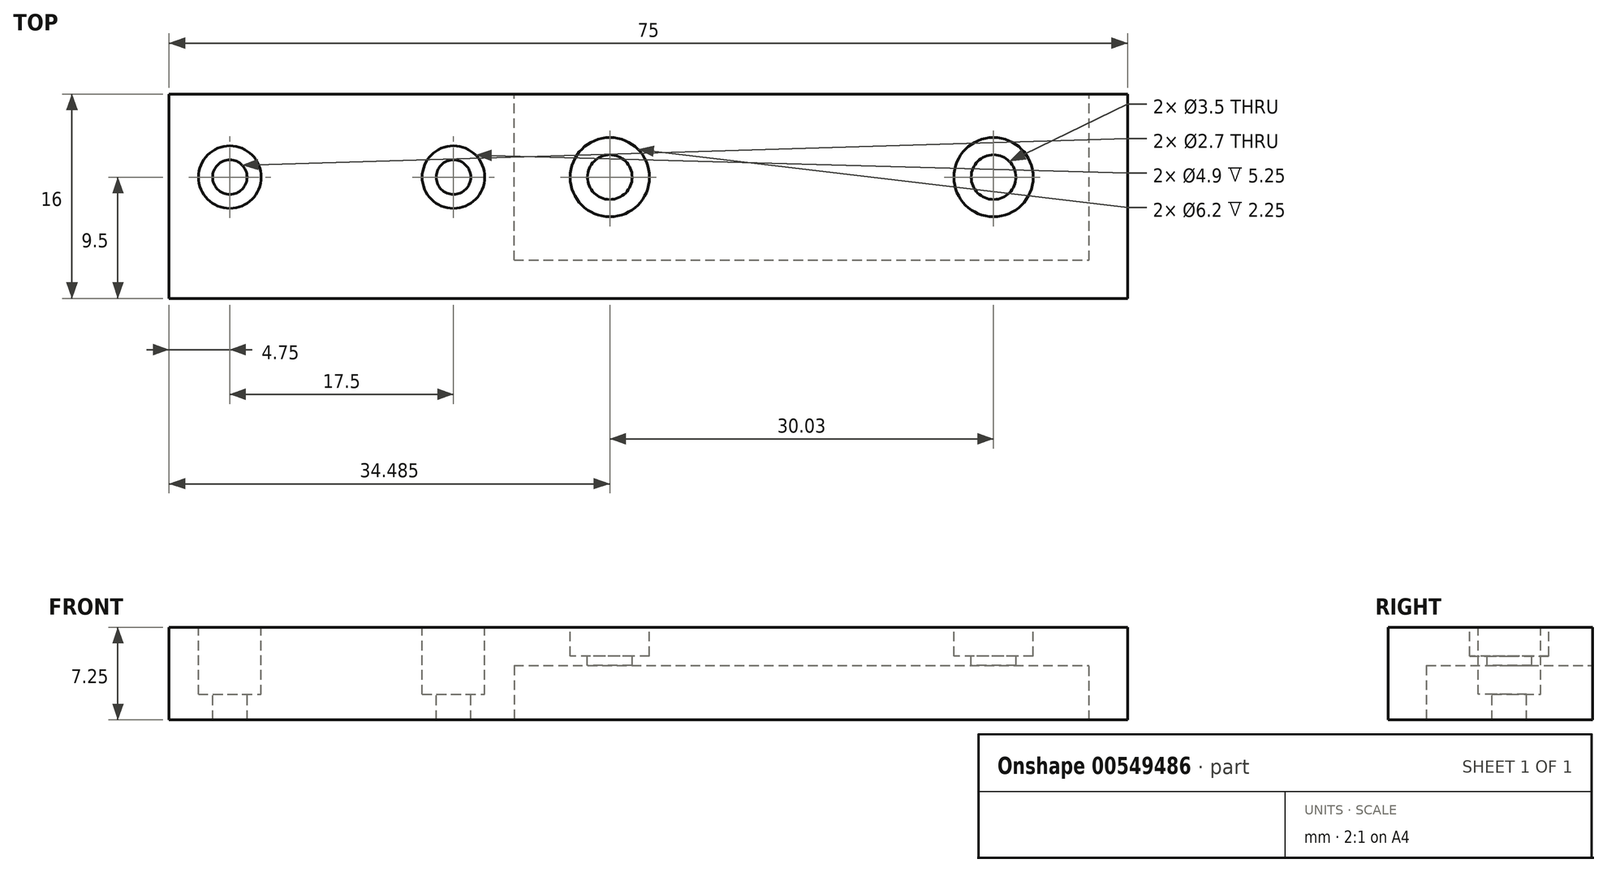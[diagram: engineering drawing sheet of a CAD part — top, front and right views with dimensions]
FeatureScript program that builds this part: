
annotation { "Feature Type Name" : "Feature", "Feature Type Description" : "" }
export const myFeature = defineFeature(function(context is Context, id is Id, definition is map)
    precondition{}
    {
        {
            var Q0;
            Q0=qCreatedBy(makeId("Front.planeOp"),FACE);
            var sketch = newSketch(context, id + "F0", { "sketchPlane" : qUnion([Q0])});
            skLineSegment(sketch, "E0", {"start": v(0, 0) * mm, "end": v(0, -4.25) * mm});
            skLineSegment(sketch, "E1", {"start": v(0, -4.25) * mm, "end": v(-27, -4.25) * mm});
            skLineSegment(sketch, "E2", {"start": v(0, 0) * mm, "end": v(45, 0) * mm});
            skLineSegment(sketch, "E3", {"start": v(45, 0) * mm, "end": v(45, 3) * mm});
            skLineSegment(sketch, "E4", {"start": v(45, 3) * mm, "end": v(0, 3) * mm});
            skLineSegment(sketch, "E5", {"start": v(0, 3) * mm, "end": v(-27, 3) * mm});
            skLineSegment(sketch, "E6", {"start": v(-27, 3) * mm, "end": v(-27, -4.25) * mm});
            skSolve(sketch);
        }
        {
            var Q0;
            Q0=makeQuery(id+"F0.imprint","IMPRINT",FACE,{"disambiguationData":[TD([[makeQuery(id+"F0.imprint","IMPRINT",EDGE,{"derivedFrom":sQuery(id+"F0.wireOp",EDGE,"E0")}),-1.0]])]});
            extrude(context, id + "F1", {"entities" : qUnion([Q0]), "depth" : 13 * mm, "offsetDistance" : 25 * mm});
        }
        {
            var Q0;
            Q0=makeQuery(id+"F1.opExtrude","SWEPT_FACE",FACE,{"disambiguationData":[OSD([sQuery(id+"F0.wireOp",EDGE,"E4"),sQuery(id+"F0.wireOp",EDGE,"E5")])]});
            var sketch = newSketch(context, id + "F2", { "sketchPlane" : qUnion([Q0])});
            skLineSegment(sketch, "E7", {"start": v(0, 0) * mm, "end": v(0, -13) * mm, "construction": true});
            skCircle(sketch, "E8", {"center": v(-22.25, -6.5) * mm, "radius": 1.35 * mm});
            skCircle(sketch, "E9", {"center": v(-4.75, -6.5) * mm, "radius": 1.35 * mm});
            skCircle(sketch, "E10", {"center": v(7.48, -6.5) * mm, "radius": 1.75 * mm});
            skCircle(sketch, "E11", {"center": v(37.52, -6.5) * mm, "radius": 1.75 * mm});
            skCircle(sketch, "E12", {"center": v(-22.25, -6.5) * mm, "radius": 2.45 * mm});
            skCircle(sketch, "E13", {"center": v(-4.75, -6.5) * mm, "radius": 2.45 * mm});
            skLineSegment(sketch, "E14", {"start": v(-4.75, -6.5) * mm, "end": v(0, -6.5) * mm, "construction": true});
            skLineSegment(sketch, "E15", {"start": v(-27, -6.5) * mm, "end": v(-22.25, -6.5) * mm, "construction": true});
            skCircle(sketch, "E16", {"center": v(7.48, -6.5) * mm, "radius": 3.1 * mm});
            skCircle(sketch, "E17", {"center": v(37.52, -6.5) * mm, "radius": 3.1 * mm});
            skLineSegment(sketch, "E18", {"start": v(0, -6.5) * mm, "end": v(7.48, -6.5) * mm, "construction": true});
            skLineSegment(sketch, "E19", {"start": v(37.52, -6.5) * mm, "end": v(45, -6.5) * mm, "construction": true});
            skSolve(sketch);
        }
        {
            var Q0;
            Q0=makeQuery(id+"F2.imprint","IMPRINT",FACE,{"disambiguationData":[TD([[makeQuery(id+"F2.imprint","IMPRINT",EDGE,{"derivedFrom":sQuery(id+"F2.wireOp",EDGE,"E9")}),1.0]])]});
            var Q1;
            Q1=makeQuery(id+"F2.imprint","IMPRINT",FACE,{"disambiguationData":[TD([[makeQuery(id+"F2.imprint","IMPRINT",EDGE,{"derivedFrom":sQuery(id+"F2.wireOp",EDGE,"E8")}),1.0]])]});
            var Q2;
            Q2=makeQuery(id+"F2.imprint","IMPRINT",FACE,{"disambiguationData":[TD([[makeQuery(id+"F2.imprint","IMPRINT",EDGE,{"derivedFrom":sQuery(id+"F2.wireOp",EDGE,"E10")}),1.0]])]});
            var Q3;
            Q3=makeQuery(id+"F2.imprint","IMPRINT",FACE,{"disambiguationData":[TD([[makeQuery(id+"F2.imprint","IMPRINT",EDGE,{"derivedFrom":sQuery(id+"F2.wireOp",EDGE,"E11")}),1.0]])]});
            extrude(context, id + "F3", {"entities" : qUnion([Q0, Q1, Q2, Q3]), "operationType" : NewBodyOperationType.REMOVE, "endBound" : BoundingType.UP_TO_NEXT, "oppositeDirection" : true, "depth" : 25 * mm, "offsetDistance" : 25 * mm});
        }
        {
            var Q0;
            Q0=makeQuery(id+"F2.imprint","IMPRINT",FACE,{"disambiguationData":[TD([[makeQuery(id+"F2.imprint","IMPRINT",EDGE,{"derivedFrom":sQuery(id+"F2.wireOp",EDGE,"E9")}),-1.0]])]});
            var Q1;
            Q1=makeQuery(id+"F2.imprint","IMPRINT",FACE,{"disambiguationData":[TD([[makeQuery(id+"F2.imprint","IMPRINT",EDGE,{"derivedFrom":sQuery(id+"F2.wireOp",EDGE,"E8")}),-1.0]])]});
            extrude(context, id + "F4", {"entities" : qUnion([Q0, Q1]), "operationType" : NewBodyOperationType.REMOVE, "endBound" : BoundingType.UP_TO_NEXT, "oppositeDirection" : true, "depth" : 25 * mm, "hasOffset" : true, "offsetDistance" : 2 * mm});
        }
        {
            var Q0;
            Q0=makeQuery(id+"F2.imprint","IMPRINT",FACE,{"disambiguationData":[TD([[makeQuery(id+"F2.imprint","IMPRINT",EDGE,{"derivedFrom":sQuery(id+"F2.wireOp",EDGE,"E10")}),-1.0]])]});
            var Q1;
            Q1=makeQuery(id+"F2.imprint","IMPRINT",FACE,{"disambiguationData":[TD([[makeQuery(id+"F2.imprint","IMPRINT",EDGE,{"derivedFrom":sQuery(id+"F2.wireOp",EDGE,"E11")}),-1.0]])]});
            extrude(context, id + "F5", {"entities" : qUnion([Q0, Q1]), "operationType" : NewBodyOperationType.REMOVE, "endBound" : BoundingType.UP_TO_NEXT, "oppositeDirection" : true, "depth" : 25 * mm, "hasOffset" : true, "offsetDistance" : 0.75 * mm});
        }
        {
            var Q0;
            Q0=makeQuery(id+"F2.imprint","IMPRINT",FACE,{"disambiguationData":[TD([[makeQuery(id+"F2.imprint","IMPRINT",EDGE,{"derivedFrom":sQuery(id+"F2.wireOp",EDGE,"E12")}),-1.0]])]});
            var sketch = newSketch(context, id + "F6", { "sketchPlane" : qUnion([Q0])});
            skLineSegment(sketch, "E20.bottom", {"start": v(-27, -13) * mm, "end": v(45, -13) * mm});
            skLineSegment(sketch, "E20.top", {"start": v(-27, -16) * mm, "end": v(45, -16) * mm});
            skLineSegment(sketch, "E20.left", {"start": v(-27, -13) * mm, "end": v(-27, -16) * mm});
            skLineSegment(sketch, "E20.right", {"start": v(45, -13) * mm, "end": v(45, -16) * mm});
            skLineSegment(sketch, "E21.bottom", {"start": v(45, -16) * mm, "end": v(48, -16) * mm});
            skLineSegment(sketch, "E21.top", {"start": v(45, 0) * mm, "end": v(48, 0) * mm});
            skLineSegment(sketch, "E21.left", {"start": v(45, -16) * mm, "end": v(45, 0) * mm});
            skLineSegment(sketch, "E21.right", {"start": v(48, -16) * mm, "end": v(48, 0) * mm});
            skSolve(sketch);
        }
        {
            var Q0;
            Q0 = qSketchRegion(id + "F6", true);
            var Q1;
            Q1=makeQuery(id+"F1.opExtrude","SWEPT_FACE",FACE,{"disambiguationData":[OSD([sQuery(id+"F0.wireOp",EDGE,"E1")])]});
            extrude(context, id + "F7", {"entities" : qUnion([Q0]), "operationType" : NewBodyOperationType.ADD, "endBound" : BoundingType.UP_TO_SURFACE, "oppositeDirection" : true, "depth" : 25 * mm, "endBoundEntityFace" : qUnion([Q1]), "offsetDistance" : 25 * mm});
        }
    });
